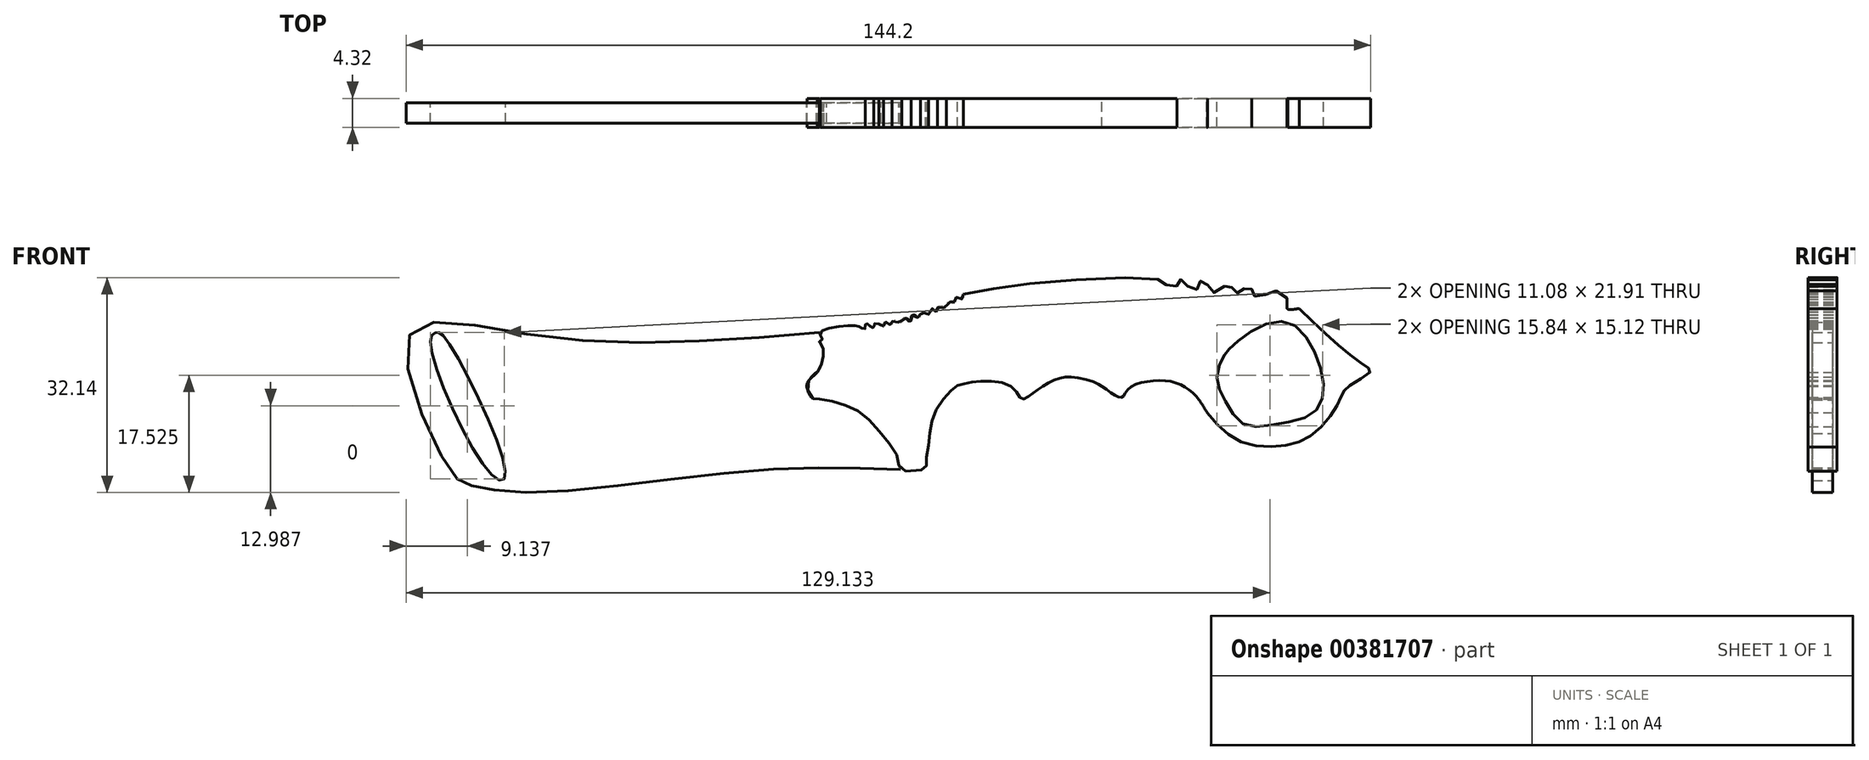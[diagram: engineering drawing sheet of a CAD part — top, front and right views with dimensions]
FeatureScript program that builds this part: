
annotation { "Feature Type Name" : "Feature", "Feature Type Description" : "" }
export const myFeature = defineFeature(function(context is Context, id is Id, definition is map)
    precondition{}
    {
        {
            var Q0;
            Q0=qCreatedBy(makeId("Front.planeOp"),FACE);
            var sketch = newSketch(context, id + "F0", { "sketchPlane" : qUnion([Q0])});
            skFitSpline(sketch, "E0", {"points": [v(8.88, -6.47) * mm, v(10.3, 1.97) * mm], "startDerivative": vector(1.42, 8.44) * mm, "endDerivative": vector(1.42, 8.44) * mm});
            skFitSpline(sketch, "E1", {"points": [v(10.3, 1.97) * mm, v(13.4, 5.58) * mm], "startDerivative": vector(3.1, 3.62) * mm, "endDerivative": vector(3.1, 3.62) * mm});
            skSolve(sketch);
        }
        {
            var Q0;
            Q0=qCreatedBy(makeId("Front.planeOp"),FACE);
            var sketch = newSketch(context, id + "F1", { "sketchPlane" : qUnion([Q0])});
            skFitSpline(sketch, "E2", {"points": [v(13.4, 5.58) * mm, v(16.49, 6.15) * mm, v(21.6, 5.3) * mm, v(23.03, 3.54) * mm, v(24.2, 4.03) * mm, v(25.6, 5.05) * mm, v(27.5, 6.19) * mm, v(29.25, 6.76) * mm, v(31.28, 6.71) * mm, v(34.13, 5.94) * mm, v(34.98, 5.45) * mm], "startDerivative": vector(22.74, 5.87) * mm, "endDerivative": vector(10.32, -7.2) * mm});
            skFitSpline(sketch, "E3", {"points": [v(34.98, 5.45) * mm, v(37.26, 3.95) * mm, v(38.13, 3.84) * mm, v(38.94, 5.05) * mm, v(41.76, 6.15) * mm, v(45.4, 6.15) * mm, v(47.84, 5.05) * mm, v(49.52, 3.4) * mm, v(50.75, 1.46) * mm], "startDerivative": vector(18.15, -13.16) * mm, "endDerivative": vector(9.16, -16.01) * mm});
            skFitSpline(sketch, "E4", {"points": [v(50.75, 1.46) * mm, v(55.54, -2.77) * mm, v(61.98, -3.49) * mm, v(66.61, -1.68) * mm, v(70.1, 2.38) * mm, v(71.03, 4.48) * mm, v(72.12, 5.58) * mm, v(75.16, 7.66) * mm, v(74.65, 8.31) * mm, v(71.03, 11) * mm, v(64.5, 17.08) * mm], "startDerivative": vector(34.42, -40.25) * mm, "endDerivative": vector(-45.75, 44.9) * mm});
            skFitSpline(sketch, "E5", {"points": [v(64.5, 17.08) * mm, v(62.7, 17.08) * mm, v(62.8, 18.18) * mm, v(62.09, 19.2) * mm, v(60.35, 19.71) * mm, v(59.22, 19) * mm, v(58.1, 18.9) * mm, v(57.38, 19.1) * mm, v(57.38, 20.12) * mm, v(56.45, 20.33) * mm, v(55.94, 19.4) * mm, v(55.12, 19.4) * mm, v(54.5, 19.71) * mm, v(54.3, 20.53) * mm, v(53.48, 20.53) * mm, v(52.56, 19.61) * mm, v(50.75, 19.82) * mm, v(50.75, 21.05) * mm, v(49.8, 21.25) * mm, v(49.5, 20.02) * mm, v(48.77, 20.02) * mm, v(47.85, 20.33) * mm, v(47.44, 21.25) * mm, v(46.32, 21.25) * mm, v(46.21, 20.53) * mm, v(45.3, 20.33) * mm, v(44.37, 20.84) * mm, v(43.76, 21.35) * mm, v(26.65, 21.05) * mm, v(14.3, 19.2) * mm], "startDerivative": vector(-64.57, -11.3) * mm, "endDerivative": vector(-104.84, -20.21) * mm});
            skFitSpline(sketch, "E6", {"points": [v(14.3, 19.2) * mm, v(14.3, 18.67) * mm, v(13.95, 18.48) * mm, v(13.4, 18.77) * mm, v(12.99, 18.5) * mm, v(12.94, 18.1) * mm, v(12.77, 17.8) * mm, v(12.21, 18.07) * mm, v(11.75, 17.78) * mm, v(11.83, 17.44) * mm, v(11.4, 17.08) * mm, v(11, 17.54) * mm, v(10.43, 17.08) * mm, v(10.45, 16.81) * mm, v(9.94, 16.64) * mm, v(9.77, 17.08) * mm, v(9.14, 16.62) * mm, v(9.07, 16.16) * mm, v(8.5, 16.3) * mm, v(8.32, 16.55) * mm, v(7.89, 16.38) * mm, v(7.86, 15.8) * mm, v(7.43, 15.75) * mm, v(7.1, 16.06) * mm, v(6.49, 15.9) * mm, v(6.49, 15.26) * mm, v(6.03, 15.26) * mm, v(5.71, 15.65) * mm, v(5.13, 15.48) * mm, v(5.06, 15.02) * mm, v(4.55, 14.97) * mm, v(4.24, 15.26) * mm, v(3.64, 15.07) * mm, v(3.59, 14.68) * mm, v(3.18, 14.7) * mm, v(3.08, 14.95) * mm, v(2.4, 15) * mm, v(2.38, 14.5) * mm, v(1.85, 14.5) * mm, v(1.63, 14.76) * mm], "startDerivative": vector(4, -21.6) * mm, "endDerivative": vector(-6.1, 13.87) * mm});
            skFitSpline(sketch, "E7", {"points": [v(49.52, 3.4) * mm, v(50.75, 9.98) * mm, v(56.38, 15) * mm, v(62.7, 17.08) * mm], "startDerivative": vector(0.74, 21.05) * mm, "endDerivative": vector(19.37, 4.65) * mm});
            skFitSpline(sketch, "E8", {"points": [v(54.06, 11) * mm, v(53.24, 9.98) * mm, v(52.18, 6.76) * mm, v(53.38, 3.4) * mm, v(56.11, -0.2) * mm, v(61.17, -0.2) * mm, v(66.61, 1.46) * mm, v(68.14, 5.05) * mm, v(66.61, 11) * mm, v(62.8, 15) * mm, v(57.61, 13.81) * mm, v(54.06, 11) * mm]});
            skFitSpline(sketch, "E9", {"points": [v(1.63, 14.76) * mm, v(0.93, 14.76) * mm, v(0.97, 14.3) * mm, v(0.55, 14.25) * mm, v(0, 14.76) * mm, v(-0.37, 14.76) * mm, v(-0.41, 14.06) * mm, v(-0.99, 14.18) * mm, v(-1.45, 14.45) * mm, v(-4.13, 14.4) * mm, v(-7.13, 13.37) * mm, v(-6.82, 12.41) * mm, v(-7.2, 12.18) * mm, v(-6.7, 11.19) * mm, v(-7.16, 8.23) * mm, v(-7.55, 7.54) * mm], "startDerivative": vector(-17.03, 3.46) * mm, "endDerivative": vector(-5.75, -8.34) * mm});
            skFitSpline(sketch, "E10", {"points": [v(-7.55, 7.54) * mm, v(-9.09, 5.58) * mm, v(-8.22, 3.59) * mm, v(-7.55, 3.54) * mm, v(-4.38, 2.92) * mm, v(-0.84, 1.28) * mm, v(2.4, -2.15) * mm, v(4.55, -5.43) * mm, v(5.04, -7.06) * mm, v(8.73, -6.8) * mm, v(8.68, -6.24) * mm, v(8.99, -3.94) * mm, v(9.35, -0.82) * mm, v(10.32, 2.05) * mm, v(12.21, 4.56) * mm, v(13.4, 5.58) * mm], "startDerivative": vector(-33.58, -26) * mm, "endDerivative": vector(21.42, 16.47) * mm});
            skSolve(sketch);
        }
        {
            var Q0;
            {var subQ2=sQuery(id+"F1.wireOp",EDGE,"E2");Q0=makeQuery(id+"F1.imprint","IMPRINT",FACE,{"disambiguationData":[TD([[makeQuery(id+"F1.imprint","IMPRINT",EDGE,{"derivedFrom":subQ2}),1.0]])]});}
            var Q1;
            {var subQ1=sQuery(id+"F1.wireOp",EDGE,"E4");Q1=makeQuery(id+"F1.imprint","IMPRINT",FACE,{"disambiguationData":[TD([[makeQuery(id+"F1.imprint","IMPRINT",EDGE,{"derivedFrom":subQ1}),1.0]])]});}
            var Q2;
            Q2 = qSketchRegion(id + "F0", true);
            extrude(context, id + "F2", {"entities" : qUnion([Q0, Q1, Q2]), "endBound" : BoundingType.SYMMETRIC, "depth" : 4.32 * mm});
        }
        {
            var Q0;
            Q0=qCreatedBy(makeId("Front.planeOp"),FACE);
            var sketch = newSketch(context, id + "F3", { "sketchPlane" : qUnion([Q0])});
            skFitSpline(sketch, "E11", {"points": [v(-7.23, 13.47) * mm, v(-49.52, 13) * mm, v(-68.6, 12.88) * mm, v(-62.6, -6.91) * mm, v(-59.42, -9.38) * mm, v(-49.52, -10.44) * mm, v(-18.19, -7.26) * mm, v(4.9, -7.03) * mm], "startDerivative": vector(-207.52, -16.94) * mm, "endDerivative": vector(137.76, -4.82) * mm});
            skFitSpline(sketch, "E12", {"points": [v(4.9, -7.03) * mm, v(4.63, -6.54) * mm, v(4.6, -5.66) * mm, v(4.2, -4.48) * mm, v(3.54, -3.53) * mm, v(2.62, -2.4) * mm, v(1.97, -1.63) * mm], "startDerivative": vector(-2.76, 3.6) * mm, "endDerivative": vector(-3.76, 4.35) * mm});
            skFitSpline(sketch, "E13", {"points": [v(1.97, -1.63) * mm, v(0.86, -0.3) * mm, v(-0.61, 1.12) * mm, v(-2.33, 2.2) * mm, v(-4.58, 3) * mm, v(-6.17, 3.42) * mm], "startDerivative": vector(-5.6, 7) * mm, "endDerivative": vector(-8.2, 2) * mm});
            skFitSpline(sketch, "E14", {"points": [v(-6.17, 3.42) * mm, v(-7.66, 3.63) * mm], "startDerivative": vector(-1.5, 0.21) * mm, "endDerivative": vector(-1.5, 0.21) * mm});
            skFitSpline(sketch, "E15", {"points": [v(-7.66, 3.63) * mm, v(-8.25, 3.63) * mm, v(-9.02, 4.9) * mm, v(-9.05, 5.94) * mm, v(-8.34, 6.91) * mm, v(-7.66, 7.53) * mm, v(-7.23, 7.84) * mm, v(-6.6, 10.27) * mm, v(-6.8, 11.55) * mm, v(-7.23, 12.14) * mm, v(-6.77, 12.4) * mm, v(-6.95, 12.83) * mm, v(-7.23, 13.47) * mm], "startDerivative": vector(-9, -2.58) * mm, "endDerivative": vector(-3.14, 9.1) * mm});
            skSolve(sketch);
        }
        {
            var Q0;
            Q0 = qSketchRegion(id + "F3", true);
            extrude(context, id + "F4", {"entities" : qUnion([Q0]), "endBound" : BoundingType.SYMMETRIC, "depth" : 3.05 * mm});
        }
        {
            var Q0;
            Q0=makeQuery(id+"F4.opExtrude","CAP_FACE",FACE,{"disambiguationData":[OSD([sQuery(id+"F3.wireOp",EDGE,"E11"),sQuery(id+"F3.wireOp",EDGE,"E12"),sQuery(id+"F3.wireOp",EDGE,"E13"),sQuery(id+"F3.wireOp",EDGE,"E14"),sQuery(id+"F3.wireOp",EDGE,"E15")])],"isStart":false});
            var sketch = newSketch(context, id + "F5", { "sketchPlane" : qUnion([Q0])});
            skFitSpline(sketch, "E16", {"points": [v(-65.42, 12.12) * mm, v(-56.06, -7.98) * mm, v(-54.2, -7.99) * mm, v(-63.3, 12.77) * mm, v(-64.63, 13.44) * mm, v(-65.42, 12.12) * mm]});
            skSolve(sketch);
        }
        {
            var Q0;
            Q0=makeQuery(id+"F5.imprint","IMPRINT",FACE,{"disambiguationData":[TD([[makeQuery(id+"F5.imprint","IMPRINT",EDGE,{"derivedFrom":sQuery(id+"F5.wireOp",EDGE,"E16")}),1.0]])]});
            extrude(context, id + "F6", {"entities" : qUnion([Q0]), "operationType" : NewBodyOperationType.REMOVE, "endBound" : BoundingType.THROUGH_ALL, "oppositeDirection" : true, "depth" : 25.4 * mm});
        }
    });
